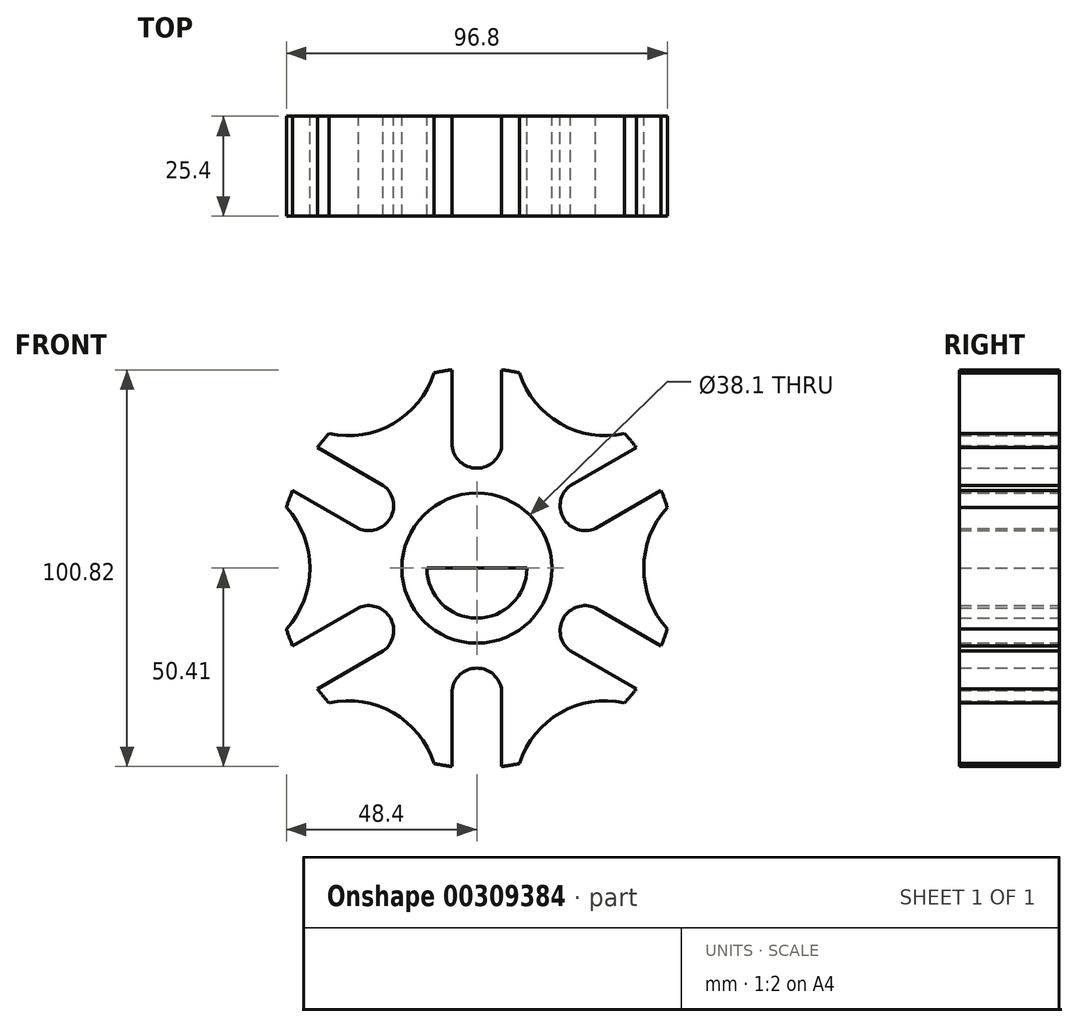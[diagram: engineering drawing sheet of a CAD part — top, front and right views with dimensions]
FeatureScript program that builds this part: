
annotation { "Feature Type Name" : "Feature", "Feature Type Description" : "" }
export const myFeature = defineFeature(function(context is Context, id is Id, definition is map)
    precondition{}
    {
        {
            var Q0;
            Q0=qCreatedBy(makeId("Front.planeOp"),FACE);
            var sketch = newSketch(context, id + "F0", { "sketchPlane" : qUnion([Q0])});
            skCircle(sketch, "E0", {"center": v(0, 0) * mm, "radius": 12.7 * mm});
            skCircle(sketch, "E1", {"center": v(0, 0) * mm, "radius": 19.05 * mm});
            skCircle(sketch, "E2", {"center": v(0, 0) * mm, "radius": 31.75 * mm, "construction": true});
            skArc(sketch, "E3", {"start": v(-6.32, 31.12) * mm, "mid": v(0, 25.4) * mm, "end": v(6.32, 31.12) * mm});
            skCircle(sketch, "E4", {"center": v(0, 0) * mm, "radius": 65.28 * mm, "construction": true});
            skLineSegment(sketch, "E5", {"start": v(-6.32, 31.12) * mm, "end": v(-6.32, 50.4) * mm});
            skLineSegment(sketch, "E6", {"start": v(6.32, 31.12) * mm, "end": v(6.32, 50.4) * mm});
            skLineSegment(sketch, "E7", {"start": v(0, 65.28) * mm, "end": v(0, -65.28) * mm});
            skLineSegment(sketch, "E8", {"start": v(-56.53, 32.64) * mm, "end": v(56.53, -32.64) * mm, "construction": true});
            skArc(sketch, "E9", {"start": v(-10.85, -49.63) * mm, "mid": v(-8.6, -50.07) * mm, "end": v(-6.32, -50.4) * mm});
            skArc(sketch, "E10", {"start": v(-48.4, -15.42) * mm, "mid": v(-42.42, 0) * mm, "end": v(-48.4, 15.42) * mm});
            skLineSegment(sketch, "E11.1.0", {"start": v(-30.1, 10.09) * mm, "end": v(-46.81, 19.73) * mm});
            skArc(sketch, "E11.1.1", {"start": v(-30.1, 10.09) * mm, "mid": v(-22, 12.7) * mm, "end": v(-23.79, 21.03) * mm});
            skLineSegment(sketch, "E11.1.2", {"start": v(-23.79, 21.03) * mm, "end": v(-40.5, 30.67) * mm});
            skLineSegment(sketch, "E11.2.0", {"start": v(-23.79, -21.03) * mm, "end": v(-40.5, -30.67) * mm});
            skArc(sketch, "E11.2.1", {"start": v(-23.79, -21.03) * mm, "mid": v(-22, -12.7) * mm, "end": v(-30.1, -10.09) * mm});
            skLineSegment(sketch, "E11.2.2", {"start": v(-30.1, -10.09) * mm, "end": v(-46.81, -19.73) * mm});
            skLineSegment(sketch, "E12.1.3.0", {"start": v(6.32, -31.12) * mm, "end": v(6.32, -50.4) * mm});
            skArc(sketch, "E12.3.3.0", {"start": v(6.32, -31.12) * mm, "mid": v(0, -25.4) * mm, "end": v(-6.32, -31.12) * mm});
            skLineSegment(sketch, "E12.7.3.0", {"start": v(-6.32, -31.12) * mm, "end": v(-6.32, -50.4) * mm});
            skLineSegment(sketch, "E12.1.4.0", {"start": v(30.1, -10.09) * mm, "end": v(46.81, -19.73) * mm});
            skArc(sketch, "E12.3.4.0", {"start": v(30.1, -10.09) * mm, "mid": v(22, -12.7) * mm, "end": v(23.79, -21.03) * mm});
            skLineSegment(sketch, "E12.7.4.0", {"start": v(23.79, -21.03) * mm, "end": v(40.5, -30.67) * mm});
            skLineSegment(sketch, "E12.1.5.0", {"start": v(23.79, 21.03) * mm, "end": v(40.5, 30.67) * mm});
            skArc(sketch, "E12.3.5.0", {"start": v(23.79, 21.03) * mm, "mid": v(22, 12.7) * mm, "end": v(30.1, 10.09) * mm});
            skLineSegment(sketch, "E12.7.5.0", {"start": v(30.1, 10.09) * mm, "end": v(46.81, 19.73) * mm});
            skArc(sketch, "E13.1.0", {"start": v(37.56, -34.2) * mm, "mid": v(21.2, -36.74) * mm, "end": v(10.85, -49.63) * mm});
            skArc(sketch, "E13.2.0", {"start": v(10.85, 49.63) * mm, "mid": v(21.2, 36.74) * mm, "end": v(37.56, 34.2) * mm});
            skArc(sketch, "E14.MirrorCS", {"start": v(-10.85, 49.63) * mm, "mid": v(-21.2, 36.74) * mm, "end": v(-37.56, 34.2) * mm});
            skArc(sketch, "E15.MirrorCS", {"start": v(-37.56, -34.2) * mm, "mid": v(-21.2, -36.74) * mm, "end": v(-10.85, -49.63) * mm});
            skArc(sketch, "E16.MirrorCS", {"start": v(48.4, -15.42) * mm, "mid": v(42.42, 0) * mm, "end": v(48.4, 15.42) * mm});
            skArc(sketch, "E17.trimOffspring", {"start": v(-40.5, -30.67) * mm, "mid": v(-39.06, -32.47) * mm, "end": v(-37.56, -34.2) * mm});
            skArc(sketch, "E18.trimOffspring", {"start": v(-48.4, -15.42) * mm, "mid": v(-47.66, -17.6) * mm, "end": v(-46.81, -19.73) * mm});
            skArc(sketch, "E19.trimOffspring", {"start": v(-46.81, 19.73) * mm, "mid": v(-47.66, 17.6) * mm, "end": v(-48.4, 15.42) * mm});
            skArc(sketch, "E20.trimOffspring", {"start": v(-37.56, 34.2) * mm, "mid": v(-39.06, 32.47) * mm, "end": v(-40.5, 30.67) * mm});
            skArc(sketch, "E21.trimOffspring", {"start": v(-6.32, 50.4) * mm, "mid": v(-8.6, 50.07) * mm, "end": v(-10.85, 49.63) * mm});
            skArc(sketch, "E22.trimOffspring", {"start": v(10.85, 49.63) * mm, "mid": v(8.6, 50.07) * mm, "end": v(6.32, 50.4) * mm});
            skArc(sketch, "E23.trimOffspring", {"start": v(40.5, 30.67) * mm, "mid": v(39.06, 32.47) * mm, "end": v(37.56, 34.2) * mm});
            skArc(sketch, "E24.trimOffspring", {"start": v(48.4, 15.42) * mm, "mid": v(47.66, 17.6) * mm, "end": v(46.81, 19.73) * mm});
            skArc(sketch, "E25.trimOffspring", {"start": v(46.81, -19.73) * mm, "mid": v(47.66, -17.6) * mm, "end": v(48.4, -15.42) * mm});
            skArc(sketch, "E26.trimOffspring", {"start": v(37.56, -34.2) * mm, "mid": v(39.06, -32.47) * mm, "end": v(40.5, -30.67) * mm});
            skArc(sketch, "E27.trimOffspring", {"start": v(6.32, -50.4) * mm, "mid": v(8.6, -50.07) * mm, "end": v(10.85, -49.63) * mm});
            skLineSegment(sketch, "E28", {"start": v(65.28, 0) * mm, "end": v(-65.28, 0) * mm});
            skSolve(sketch);
        }
        {
            var Q0;
            Q0 = qSketchRegion(id + "F0", true);
            extrude(context, id + "F1", {"entities" : qUnion([Q0]), "depth" : 25.4 * mm});
        }
        {
            var Q0;
            {var subQ0=sQuery(id+"F0.wireOp",EDGE,"E28");var subQ1=sQuery(id+"F0.wireOp",EDGE,"E0");var subQ2=makeQuery(id+"F0.imprint","INTERSECT",VERTEX,{"disambiguationData":[OD(1.0)],"derivedFrom":[subQ1,subQ0]});Q0=makeQuery(id+"F0.imprint","IMPRINT",FACE,{"disambiguationData":[TD([[makeQuery(id+"F0.imprint","IMPRINT",EDGE,{"disambiguationData":[TD([[subQ2,-1.0]])],"derivedFrom":subQ1}),1.0]])]});}
            var Q1;
            {var subQ0=sQuery(id+"F0.wireOp",EDGE,"E7");var subQ1=sQuery(id+"F0.wireOp",EDGE,"E0");var subQ2=makeQuery(id+"F0.imprint","INTERSECT",VERTEX,{"disambiguationData":[OD(0.0)],"derivedFrom":[subQ1,subQ0]});Q1=makeQuery(id+"F0.imprint","IMPRINT",FACE,{"disambiguationData":[TD([[makeQuery(id+"F0.imprint","IMPRINT",EDGE,{"disambiguationData":[TD([[subQ2,-1.0]])],"derivedFrom":subQ1}),1.0]])]});}
            var Q2;
            {var subQ0=sQuery(id+"F0.wireOp",EDGE,"E7");var subQ1=sQuery(id+"F0.wireOp",EDGE,"E0");var subQ2=makeQuery(id+"F0.imprint","INTERSECT",VERTEX,{"disambiguationData":[OD(0.0)],"derivedFrom":[subQ1,subQ0]});Q2=makeQuery(id+"F0.imprint","IMPRINT",FACE,{"disambiguationData":[TD([[makeQuery(id+"F0.imprint","IMPRINT",EDGE,{"disambiguationData":[TD([[subQ2,1.0]])],"derivedFrom":subQ1}),1.0]])]});}
            var Q3;
            {var subQ0=sQuery(id+"F0.wireOp",EDGE,"E28");var subQ1=sQuery(id+"F0.wireOp",EDGE,"E0");var subQ2=makeQuery(id+"F0.imprint","INTERSECT",VERTEX,{"disambiguationData":[OD(0.0)],"derivedFrom":[subQ1,subQ0]});Q3=makeQuery(id+"F0.imprint","IMPRINT",FACE,{"disambiguationData":[TD([[makeQuery(id+"F0.imprint","IMPRINT",EDGE,{"disambiguationData":[TD([[subQ2,1.0]])],"derivedFrom":subQ1}),1.0]])]});}
            extrude(context, id + "F2", {"entities" : qUnion([Q0, Q1, Q2, Q3]), "depth" : 25.4 * mm});
        }
    });
